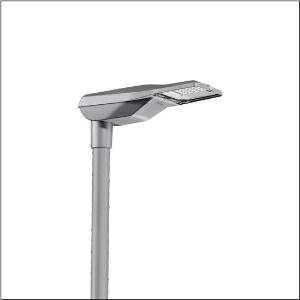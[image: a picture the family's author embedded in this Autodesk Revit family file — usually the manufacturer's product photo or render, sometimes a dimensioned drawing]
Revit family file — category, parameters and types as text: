
# Revit family: streetlight_sl_21_iq_micro___stw1_0a_5xe1e41d08db_39eb
name_source: partatom
category: Lighting Fixtures
units: mm (PartAtom-declared; Revit-internal decimal feet)

## family parameters
Cut with Voids When Loaded = No
Host = Face
Light Source = No
Part Type = Normal
Room Calculation Point = No
Round Connector Dimension = Use Diameter
Shared = No

## types (1)
- --- (1 x LED, 5010 lm, 36.4 W, 4000K)
    Apparent Load = 36 VA
    CIE Flux Codes = 38 75 98 100 100
    Color Rendering = 70
    Color Temperature = 4000K
    Default Elevation = 1800 mm
    Description = Streetlight SL 21 iQ micro, mast luminaire, primary light control with lens, of PMMA, primary optical cover: cover, of toughened safety glass, transparent, light distribution: STW1.0a, light emission: direct distribution, primary light characteristic: asymmetric, installation type: post-top, side-entry, LED, High Power LED, rated luminous flux: 5.010lm, luminous efficacy: 138lm/W, light colour: 740, colour temperature: 4000K, control: Auto-Match, Temp-Guard, Lumen-Switch, Night-Set, Smart-Wire, Light-Fading, Desk-Remote (wireless, voltage-free reading and setting of iQ features in the workshop via application-optimized NFC function/RFID function), optimised constant luminous flux control (CLO 2.0), presetting dimming linear, mains connection: 220..240V, AC, 50/60Hz, start of lifetime: 36W, end of service life: 38W, reduction: 16W, luminaire housing, of diecast aluminium, powder-coated, Siteco® metallic grey (DB 702S), corrosivity category C5 mid according to DIN EN ISO 12944, please order mast flange separately, inclination adjustable: 0°, 5°, 10°, 15°, sealing non-destructively replaceable, multi-level sealing system, length: 528mm, width: 235mm, height: 110mm, mast flange for spigot size: 42mm (side-entry): 5XC10008XM4, 60/48mm (side-entry/post-top): 5XC10108XM2, 76/60mm (side-entry/post-top): 5XC10108XM1, protection rating (complete): IP66, insulation class (complete): insulation class II (safety insulation), certification: CE, ENEC, ENEC+, VDE, impact resistance: IK09, permissible operating ambient temperature for outdoor applications: -40..+50°C, standard-compliant lighting for roads and squares, packaging unit: 1 piece

Light Distribution: STW1.0a
    Height = 110 mm
    Lamp = 1 x LED
    Lamp Light Flux = 5010 lm
    Lamp Power = 36.4 W
    Lamp count = 1
    Length = 528 mm
    Luminous efficacy = 138 lm/W
    Manufacturer = Siteco
    ModVariant = No
    Model = 5XE1E41D08DB
    Number of Poles = 1
    OnlyDefault = Yes
    Power Factor = 1
    Product Name = Streetlight SL 21 iQ micro | STW1.0a
    Product group = mast luminaire | pylon top
    ProductGroupID = 6100
    Protection Class = Protection class II
    Protection Degree = IP 66
    RLX_Detail_Level = 1
    RLX_Emergency_Light_Flux = 0 lm
    RLX_Emergency_Type = 0
    RLX_Emergency_Type_DB = No
    RlxData = <blob elided: 98853 chars, md5=d37050f6>
    Socket = socket
    Standby Power = 0 W
    System Light Flux = 5010 lm
    System Power = 36 W
    Type Comments = factory setting: luminous flux: 100 % | dim-lin: 254 | 715 mA
    Type Image = l_1006881.jpg
    URL = http://relux.com
    VarID = @adj_087727
    Voltage = 0 V
    Weight = 0.00 kg
    Width = 235 mm

## geometry (parser evidence)
native form markers: Blend x4, Sweep x10
no freeform markers — native parametric forms only
